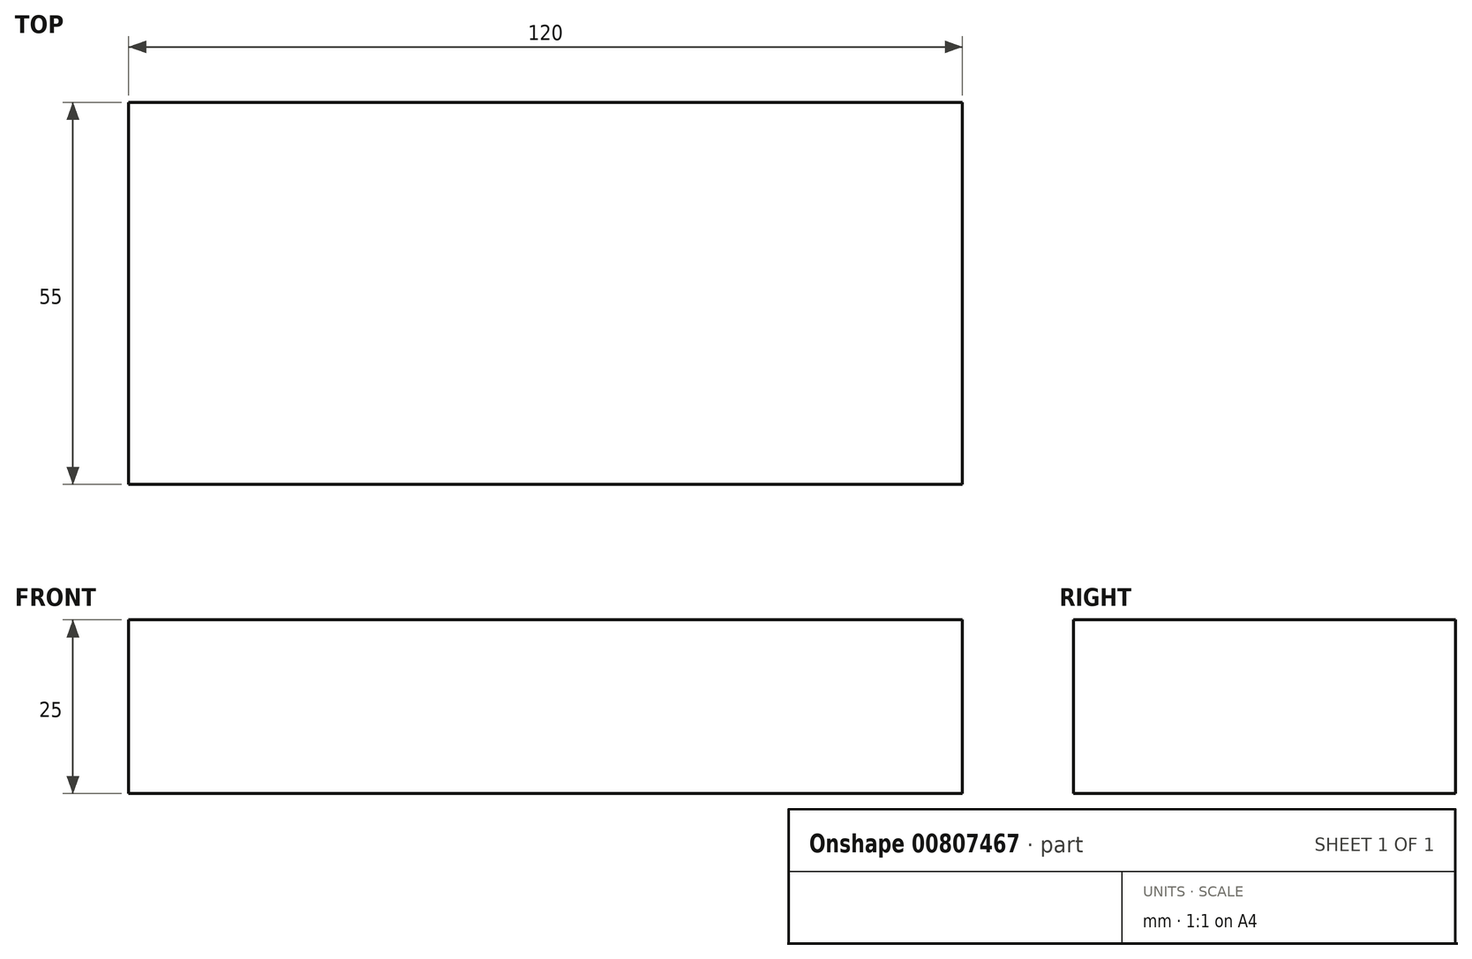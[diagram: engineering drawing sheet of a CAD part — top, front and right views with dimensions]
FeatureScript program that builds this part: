
annotation { "Feature Type Name" : "Feature", "Feature Type Description" : "" }
export const myFeature = defineFeature(function(context is Context, id is Id, definition is map)
    precondition{}
    {
        {
            var Q0;
            Q0=qCreatedBy(makeId("Front.planeOp"),FACE);
            var sketch = newSketch(context, id + "F0", { "sketchPlane" : qUnion([Q0])});
            skLineSegment(sketch, "E0.bottom", {"start": v(-60, 12.5) * mm, "end": v(60, 12.5) * mm});
            skLineSegment(sketch, "E0.top", {"start": v(-60, -12.5) * mm, "end": v(60, -12.5) * mm});
            skLineSegment(sketch, "E0.left", {"start": v(-60, 12.5) * mm, "end": v(-60, -12.5) * mm});
            skLineSegment(sketch, "E0.right", {"start": v(60, 12.5) * mm, "end": v(60, -12.5) * mm});
            skPoint(sketch, "E0.middle", {"position": v(0, 0) * mm});
            skSolve(sketch);
        }
        {
            var Q0;
            Q0=makeQuery(id+"F0.imprint","IMPRINT",FACE,{"disambiguationData":[TD([[makeQuery(id+"F0.imprint","IMPRINT",EDGE,{"derivedFrom":sQuery(id+"F0.wireOp",EDGE,"E0.bottom")}),-1.0]])]});
            extrude(context, id + "F1", {"entities" : qUnion([Q0]), "depth" : 55 * mm, "offsetDistance" : 25.4 * mm});
        }
    });
